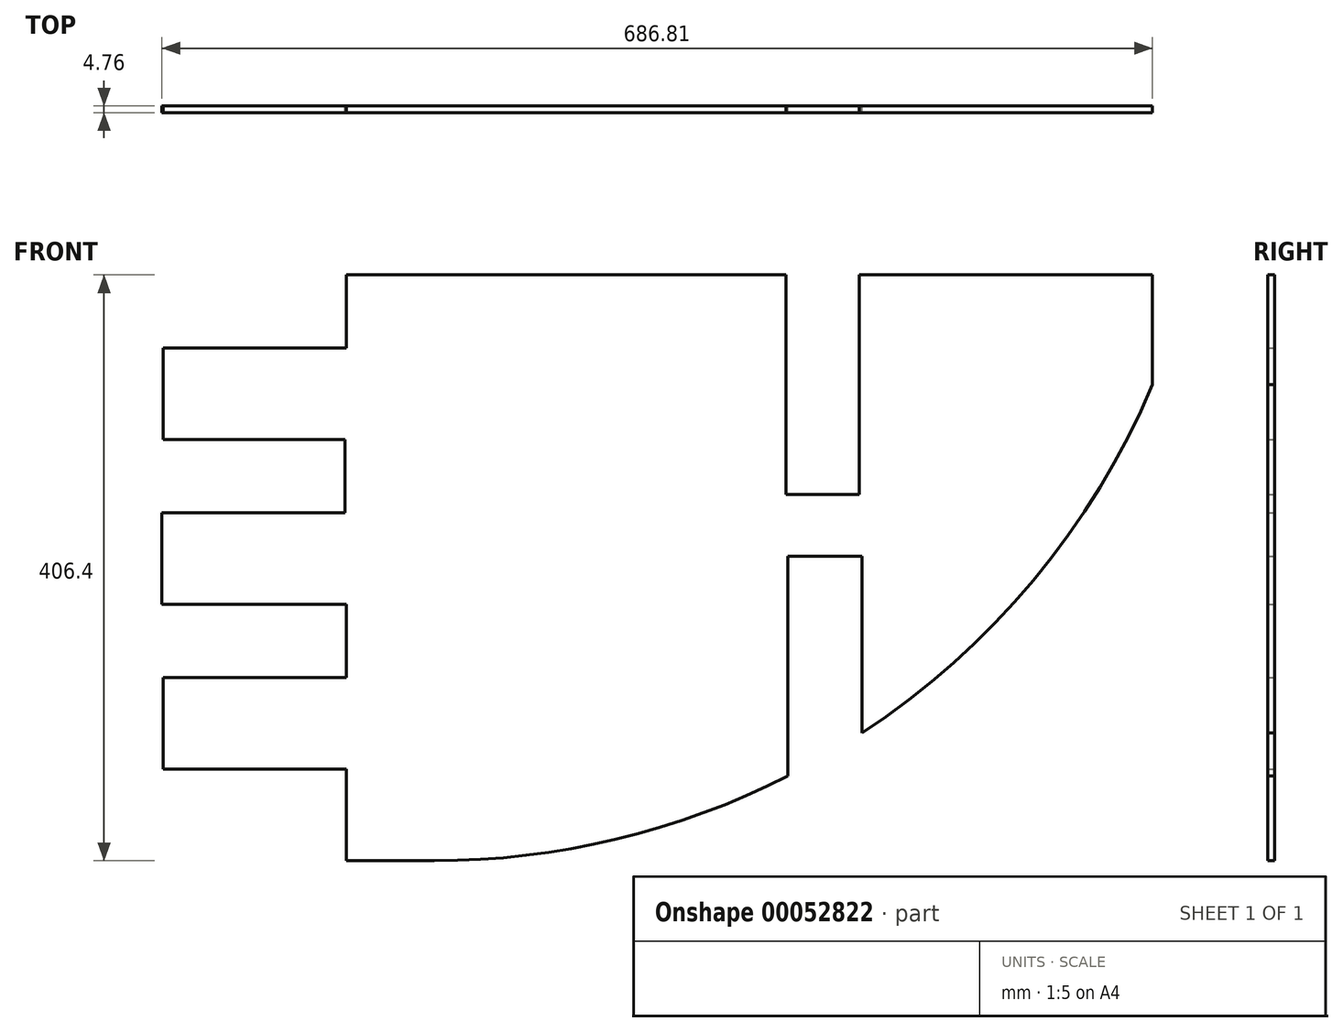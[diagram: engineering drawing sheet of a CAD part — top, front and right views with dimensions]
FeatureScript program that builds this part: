
annotation { "Feature Type Name" : "Feature", "Feature Type Description" : "" }
export const myFeature = defineFeature(function(context is Context, id is Id, definition is map)
    precondition{}
    {
        {
            var Q0;
            Q0=qCreatedBy(makeId("Front.planeOp"),FACE);
            var sketch = newSketch(context, id + "F0", { "sketchPlane" : qUnion([Q0])});
            skLineSegment(sketch, "E0", {"start": v(0, -406.4) * mm, "end": v(0, -342.9) * mm});
            skLineSegment(sketch, "E1", {"start": v(0, -50.8) * mm, "end": v(-127, -50.8) * mm});
            skLineSegment(sketch, "E2", {"start": v(-127, -50.8) * mm, "end": v(-127, -114.3) * mm});
            skLineSegment(sketch, "E3", {"start": v(-127, -114.3) * mm, "end": v(-1, -114.3) * mm});
            skLineSegment(sketch, "E4", {"start": v(-1, -165.1) * mm, "end": v(-128, -165.1) * mm});
            skLineSegment(sketch, "E5", {"start": v(-128, -165.1) * mm, "end": v(-128, -228.6) * mm});
            skLineSegment(sketch, "E6", {"start": v(-128, -228.6) * mm, "end": v(0, -228.6) * mm});
            skLineSegment(sketch, "E7", {"start": v(0, -279.4) * mm, "end": v(-127, -279.4) * mm});
            skLineSegment(sketch, "E8", {"start": v(-127, -279.4) * mm, "end": v(-127, -342.9) * mm});
            skLineSegment(sketch, "E9", {"start": v(-127, -342.9) * mm, "end": v(0, -342.9) * mm});
            skLineSegment(sketch, "E10.trimOffspring", {"start": v(0, -50.8) * mm, "end": v(0, 0) * mm});
            skLineSegment(sketch, "E11", {"start": v(0, 0) * mm, "end": v(304.8, 0) * mm});
            skLineSegment(sketch, "E12", {"start": v(558.8, 0) * mm, "end": v(558.8, -76.2) * mm});
            skLineSegment(sketch, "E13", {"start": v(0, -406.4) * mm, "end": v(60.96, -406.4) * mm});
            skArc(sketch, "E14", {"start": v(60.96, -406.4) * mm, "mid": v(186.87, -391.53) * mm, "end": v(305.85, -347.73) * mm});
            skPoint(sketch, "E15.start.orphan", {"position": v(-558.8, 0) * mm});
            skLineSegment(sketch, "E16", {"start": v(-1, -114.3) * mm, "end": v(-1, -165.1) * mm});
            skLineSegment(sketch, "E17", {"start": v(0, -228.6) * mm, "end": v(0, -279.4) * mm});
            skLineSegment(sketch, "E18", {"start": v(304.8, 0) * mm, "end": v(304.8, -152.4) * mm});
            skLineSegment(sketch, "E19", {"start": v(304.8, -152.4) * mm, "end": v(355.6, -152.4) * mm});
            skLineSegment(sketch, "E20", {"start": v(355.6, -152.4) * mm, "end": v(355.6, 0) * mm});
            skLineSegment(sketch, "E21.trimOffspring", {"start": v(355.6, 0) * mm, "end": v(558.8, 0) * mm});
            skLineSegment(sketch, "E22", {"start": v(305.85, -347.73) * mm, "end": v(305.85, -195.33) * mm});
            skLineSegment(sketch, "E23", {"start": v(305.85, -195.33) * mm, "end": v(357.41, -195.33) * mm});
            skLineSegment(sketch, "E24", {"start": v(357.41, -195.33) * mm, "end": v(357.41, -317.83) * mm});
            skArc(sketch, "E25.trimOffspring", {"start": v(357.41, -317.83) * mm, "mid": v(476.08, -211.99) * mm, "end": v(558.8, -76.2) * mm});
            skSolve(sketch);
        }
        {
            var Q0;
            Q0=makeQuery(id+"F0.imprint","IMPRINT",FACE,{"disambiguationData":[TD([[makeQuery(id+"F0.imprint","IMPRINT",EDGE,{"derivedFrom":sQuery(id+"F0.wireOp",EDGE,"E0")}),-1.0]])]});
            extrude(context, id + "F1", {"entities" : qUnion([Q0]), "depth" : 4.76 * mm});
        }
    });
